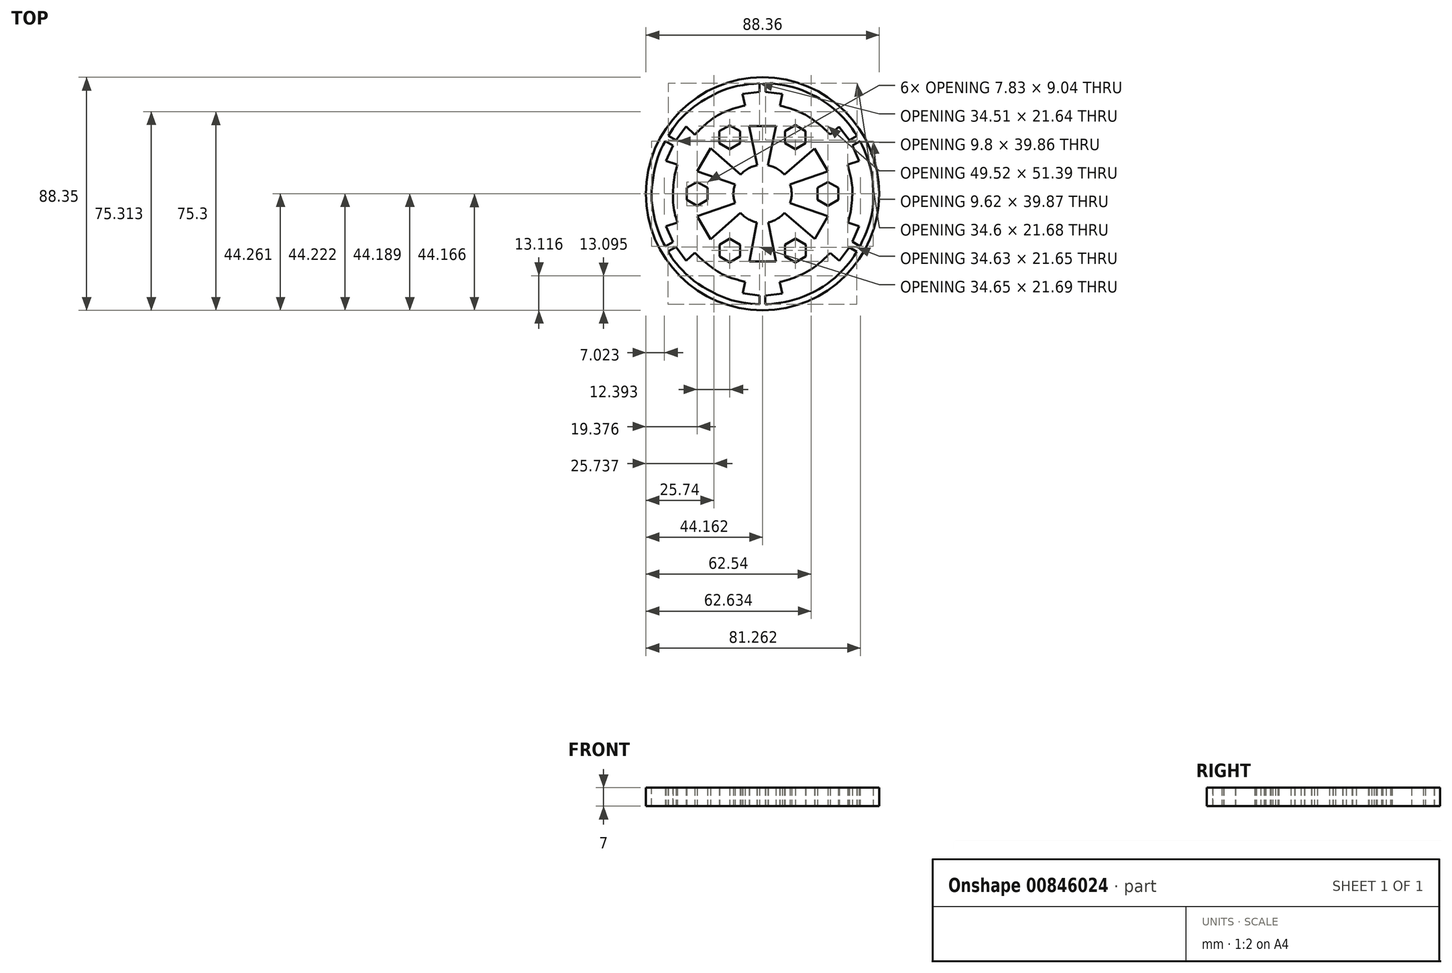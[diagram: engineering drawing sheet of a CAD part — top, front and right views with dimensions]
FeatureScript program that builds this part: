
annotation { "Feature Type Name" : "Feature", "Feature Type Description" : "" }
export const myFeature = defineFeature(function(context is Context, id is Id, definition is map)
    precondition{}
    {
        {
            var Q0;
            Q0=qCreatedBy(makeId("Top.planeOp"),FACE);
            var sketch = newSketch(context, id + "F0", { "sketchPlane" : qUnion([Q0])});
            skLineSegment(sketch, "E0", {"start": v(2.42, -11.3) * mm, "end": v(4.95, -23.85) * mm});
            skLineSegment(sketch, "E1", {"start": v(-2.75, -11.3) * mm, "end": v(-5.12, -23.88) * mm});
            skLineSegment(sketch, "E2", {"start": v(-5.12, -23.88) * mm, "end": v(4.95, -23.85) * mm});
            skLineSegment(sketch, "E3", {"start": v(-10.32, -6.91) * mm, "end": v(-19.92, -15.41) * mm});
            skLineSegment(sketch, "E4", {"start": v(-12.85, -2.44) * mm, "end": v(-24.96, -6.66) * mm});
            skLineSegment(sketch, "E5", {"start": v(-24.96, -6.66) * mm, "end": v(-19.92, -15.41) * mm});
            skLineSegment(sketch, "E6", {"start": v(12.49, -2.45) * mm, "end": v(24.56, -6.66) * mm});
            skLineSegment(sketch, "E7", {"start": v(9.9, -6.97) * mm, "end": v(19.6, -15.3) * mm});
            skLineSegment(sketch, "E8", {"start": v(19.6, -15.3) * mm, "end": v(24.56, -6.66) * mm});
            skLineSegment(sketch, "E9", {"start": v(12.44, 6.2) * mm, "end": v(24.56, 10.39) * mm});
            skLineSegment(sketch, "E10", {"start": v(9.84, 10.64) * mm, "end": v(19.52, 19.04) * mm});
            skLineSegment(sketch, "E11", {"start": v(19.52, 19.04) * mm, "end": v(24.56, 10.39) * mm});
            skLineSegment(sketch, "E12", {"start": v(2.36, 14.93) * mm, "end": v(4.87, 27.52) * mm});
            skLineSegment(sketch, "E13", {"start": v(-2.72, 14.93) * mm, "end": v(-5.3, 27.49) * mm});
            skLineSegment(sketch, "E14", {"start": v(-5.3, 27.49) * mm, "end": v(4.87, 27.52) * mm});
            skLineSegment(sketch, "E15", {"start": v(-10.25, 10.6) * mm, "end": v(-19.89, 19.07) * mm});
            skLineSegment(sketch, "E16", {"start": v(-12.8, 6.18) * mm, "end": v(-24.92, 10.37) * mm});
            skLineSegment(sketch, "E17", {"start": v(-24.92, 10.37) * mm, "end": v(-19.89, 19.07) * mm});
            skLineSegment(sketch, "E18", {"start": v(-1.37, 43.75) * mm, "end": v(-1.37, 40.4) * mm});
            skLineSegment(sketch, "E19", {"start": v(0.97, 43.78) * mm, "end": v(0.97, 40.4) * mm});
            skLineSegment(sketch, "E20", {"start": v(33.82, 20.11) * mm, "end": v(36.73, 21.82) * mm});
            skLineSegment(sketch, "E21", {"start": v(33.82, -16.36) * mm, "end": v(36.72, -18.04) * mm});
            skLineSegment(sketch, "E22", {"start": v(32.7, -18.45) * mm, "end": v(35.5, -20.13) * mm});
            skLineSegment(sketch, "E23", {"start": v(-33, -18.4) * mm, "end": v(-35.94, -20.06) * mm});
            skLineSegment(sketch, "E24", {"start": v(-37.04, -18.08) * mm, "end": v(-34.11, -16.4) * mm});
            skLineSegment(sketch, "E25", {"start": v(-37.05, 21.78) * mm, "end": v(-34.1, 20.13) * mm});
            skLineSegment(sketch, "E26", {"start": v(-35.88, 23.84) * mm, "end": v(-32.98, 22.11) * mm});
            skLineSegment(sketch, "E27", {"start": v(-34.1, 20.13) * mm, "end": v(-36.74, 14.27) * mm});
            skLineSegment(sketch, "E28", {"start": v(-36.74, 14.27) * mm, "end": v(-32.44, 12.84) * mm});
            skLineSegment(sketch, "E29", {"start": v(-32.98, 22.11) * mm, "end": v(-29.18, 27.3) * mm});
            skLineSegment(sketch, "E30", {"start": v(-29.18, 27.3) * mm, "end": v(-25.86, 24.23) * mm});
            skLineSegment(sketch, "E31", {"start": v(-34.11, -16.4) * mm, "end": v(-36.73, -10.52) * mm});
            skLineSegment(sketch, "E32", {"start": v(-36.73, -10.52) * mm, "end": v(-32.44, -9.07) * mm});
            skLineSegment(sketch, "E33", {"start": v(-33, -18.4) * mm, "end": v(-29.14, -23.57) * mm});
            skLineSegment(sketch, "E34", {"start": v(-29.14, -23.57) * mm, "end": v(-25.78, -20.54) * mm});
            skPoint(sketch, "E35.end.orphan", {"position": v(-1.46, -40.1) * mm});
            skPoint(sketch, "E35.start.orphan", {"position": v(-1.46, -36.72) * mm});
            skLineSegment(sketch, "E36", {"start": v(-1.3, -36.72) * mm, "end": v(-1.3, -40.1) * mm});
            skPoint(sketch, "E37.end.orphan", {"position": v(1.01, -40.1) * mm});
            skPoint(sketch, "E37.start.orphan", {"position": v(1.01, -36.72) * mm});
            skLineSegment(sketch, "E38", {"start": v(-1.3, -36.72) * mm, "end": v(-1.46, -36.72) * mm});
            skLineSegment(sketch, "E39", {"start": v(-1.3, -36.72) * mm, "end": v(-7.67, -35.94) * mm});
            skLineSegment(sketch, "E40", {"start": v(-7.67, -35.94) * mm, "end": v(-6.75, -31.52) * mm});
            skLineSegment(sketch, "E41", {"start": v(0.86, -36.72) * mm, "end": v(0.86, -40.1) * mm});
            skLineSegment(sketch, "E42", {"start": v(0.86, -36.72) * mm, "end": v(7.25, -36.02) * mm});
            skLineSegment(sketch, "E43", {"start": v(7.25, -36.02) * mm, "end": v(6.34, -31.59) * mm});
            skLineSegment(sketch, "E44", {"start": v(32.7, -18.45) * mm, "end": v(28.86, -23.6) * mm});
            skLineSegment(sketch, "E45", {"start": v(28.86, -23.6) * mm, "end": v(25.42, -20.65) * mm});
            skLineSegment(sketch, "E46", {"start": v(33.82, -16.36) * mm, "end": v(36.44, -10.53) * mm});
            skLineSegment(sketch, "E47", {"start": v(36.44, -10.53) * mm, "end": v(32.16, -9.1) * mm});
            skLineSegment(sketch, "E48", {"start": v(33.82, 20.11) * mm, "end": v(36.4, 14.22) * mm});
            skLineSegment(sketch, "E49", {"start": v(36.4, 14.22) * mm, "end": v(32.1, 12.82) * mm});
            skLineSegment(sketch, "E50", {"start": v(32.66, 22.1) * mm, "end": v(35.58, 23.8) * mm});
            skLineSegment(sketch, "E51", {"start": v(32.66, 22.1) * mm, "end": v(28.81, 27.25) * mm});
            skLineSegment(sketch, "E52", {"start": v(28.81, 27.25) * mm, "end": v(25.43, 24.28) * mm});
            skLineSegment(sketch, "E53", {"start": v(-1.37, 40.4) * mm, "end": v(-7.76, 39.67) * mm});
            skLineSegment(sketch, "E54", {"start": v(-7.76, 39.67) * mm, "end": v(-6.8, 35.25) * mm});
            skLineSegment(sketch, "E55", {"start": v(0.97, 40.4) * mm, "end": v(7.35, 39.66) * mm});
            skLineSegment(sketch, "E56", {"start": v(7.35, 39.66) * mm, "end": v(6.4, 35.21) * mm});
            skFitSpline(sketch, "E57", {"points": [v(-32.44, -9.07) * mm, v(-33.84, -3.63) * mm, v(-34.08, 1.8) * mm, v(-33.72, 7.26) * mm, v(-32.44, 12.84) * mm], "startDerivative": vector(-6.71, 21.57) * mm, "endDerivative": vector(5.92, 22) * mm});
            skFitSpline(sketch, "E58", {"points": [v(-25.86, 24.23) * mm, v(-21.86, 28.08) * mm, v(-17.87, 31.1) * mm, v(-11.94, 33.88) * mm, v(-6.8, 35.25) * mm], "startDerivative": vector(16.19, 16.08) * mm, "endDerivative": vector(20.55, 4.51) * mm});
            skFitSpline(sketch, "E59", {"points": [v(-25.78, -20.54) * mm, v(-22.24, -23.88) * mm, v(-17.88, -27.2) * mm, v(-13.06, -29.7) * mm, v(-6.75, -31.52) * mm], "startDerivative": vector(14.21, -15.18) * mm, "endDerivative": vector(24.22, -5.87) * mm});
            skFitSpline(sketch, "E60", {"points": [v(6.34, -31.59) * mm, v(10.25, -30.54) * mm, v(15, -28.56) * mm, v(19.43, -26) * mm, v(22.3, -23.6) * mm, v(25.42, -20.65) * mm], "startDerivative": vector(20.1, 4.76) * mm, "endDerivative": vector(16.26, 15.48) * mm});
            skFitSpline(sketch, "E61", {"points": [v(32.16, -9.1) * mm, v(33.4, -3.73) * mm, v(33.82, 1.8) * mm, v(33.82, 4.02) * mm, v(33.31, 7.64) * mm, v(32.1, 12.82) * mm], "startDerivative": vector(6.39, 22.77) * mm, "endDerivative": vector(-6.09, 23.91) * mm});
            skFitSpline(sketch, "E62", {"points": [v(25.43, 24.28) * mm, v(21.95, 27.65) * mm, v(17.67, 30.77) * mm, v(13.95, 32.78) * mm, v(8.52, 34.72) * mm, v(6.4, 35.21) * mm], "startDerivative": vector(-15.56, 16.18) * mm, "endDerivative": vector(-12.9, 2.5) * mm});
            skFitSpline(sketch, "E63", {"points": [v(-35.88, 23.84) * mm, v(-32.44, 28.82) * mm, v(-28.06, 33.25) * mm, v(-23.94, 36.4) * mm, v(-17.87, 39.84) * mm, v(-10.6, 42.49) * mm, v(-1.37, 43.75) * mm], "startDerivative": vector(20.42, 32.39) * mm, "endDerivative": vector(49.13, 4.55) * mm});
            skFitSpline(sketch, "E64", {"points": [v(-37.05, 21.78) * mm, v(-39.75, 16.01) * mm, v(-41.55, 8.23) * mm, v(-42.24, 1.8) * mm, v(-41.64, -4.95) * mm, v(-39.28, -13.47) * mm, v(-37.04, -18.08) * mm], "startDerivative": vector(-18.3, -33.84) * mm, "endDerivative": vector(15.88, -28.7) * mm});
            skFitSpline(sketch, "E65", {"points": [v(-35.94, -20.06) * mm, v(-34.25, -22.77) * mm, v(-31.48, -26.18) * mm, v(-26.4, -30.97) * mm, v(-19.92, -35.06) * mm, v(-13, -38.17) * mm, v(-6.85, -39.55) * mm, v(-1.3, -40.1) * mm], "startDerivative": vector(15, -25.38) * mm, "endDerivative": vector(39.5, -3.13) * mm});
            skPoint(sketch, "E66.1.internal.orphan", {"position": v(2.63, -40.1) * mm});
            skPoint(sketch, "E66.5.internal.orphan", {"position": v(24.36, -32.35) * mm});
            skPoint(sketch, "E66.7.internal.orphan", {"position": v(32.54, -24.74) * mm});
            skFitSpline(sketch, "E67", {"points": [v(0.86, -40.1) * mm, v(2.15, -40.1) * mm, v(5.92, -39.6) * mm, v(9.73, -38.86) * mm, v(14.05, -37.67) * mm, v(19.35, -35.31) * mm, v(23.5, -32.88) * mm, v(27.01, -30.18) * mm, v(30.99, -26.24) * mm, v(33.04, -23.8) * mm, v(35.5, -20.13) * mm], "startDerivative": vector(19.64, -0.97) * mm, "endDerivative": vector(24.32, 37.94) * mm});
            skFitSpline(sketch, "E68", {"points": [v(0.97, 43.78) * mm, v(7.81, 43.04) * mm, v(14.15, 41.33) * mm, v(20.52, 38.42) * mm, v(26.43, 34.35) * mm, v(32, 28.84) * mm, v(35.58, 23.8) * mm], "startDerivative": vector(41.76, -3.24) * mm, "endDerivative": vector(20.77, -31.79) * mm});
            skFitSpline(sketch, "E69", {"points": [v(36.73, 21.82) * mm, v(39.5, 15.56) * mm, v(41.34, 8.48) * mm, v(41.7, 3.2) * mm, v(41.6, -2.96) * mm, v(39.98, -10.44) * mm, v(36.72, -18.04) * mm], "startDerivative": vector(17.68, -36.35) * mm, "endDerivative": vector(-19.56, -41.17) * mm});
            skCircle(sketch, "E70", {"center": v(-0.18, 1.8) * mm, "radius": 44.18 * mm});
            skLineSegment(sketch, "E71", {"start": v(10.23, 5.43) * mm, "end": v(10.17, 5.4) * mm});
            skLineSegment(sketch, "E72", {"start": v(8.08, 9.11) * mm, "end": v(8.03, 9.07) * mm});
            skLineSegment(sketch, "E73", {"start": v(-2.25, 12.63) * mm, "end": v(-2.24, 12.57) * mm});
            skLineSegment(sketch, "E74", {"start": v(1.9, 12.63) * mm, "end": v(1.9, 12.57) * mm});
            skLineSegment(sketch, "E75", {"start": v(-8.5, 9.05) * mm, "end": v(-8.45, 9.01) * mm});
            skLineSegment(sketch, "E76", {"start": v(-10.6, 5.42) * mm, "end": v(-10.54, 5.4) * mm});
            skLineSegment(sketch, "E77", {"start": v(-10.64, -1.67) * mm, "end": v(-10.58, -1.65) * mm});
            skLineSegment(sketch, "E78", {"start": v(-8.56, -5.36) * mm, "end": v(-8.52, -5.32) * mm});
            skLineSegment(sketch, "E79", {"start": v(-2.31, -9.01) * mm, "end": v(-2.3, -8.95) * mm});
            skLineSegment(sketch, "E80", {"start": v(1.96, -9) * mm, "end": v(1.95, -8.95) * mm});
            skLineSegment(sketch, "E81", {"start": v(8.12, -5.44) * mm, "end": v(8.08, -5.4) * mm});
            skLineSegment(sketch, "E82", {"start": v(10.28, -1.68) * mm, "end": v(10.22, -1.66) * mm});
            skCircle(sketch, "E83", {"center": v(-0.18, 1.8) * mm, "radius": 11.03 * mm});
            skLineSegment(sketch, "E84", {"start": v(-10.25, 10.6) * mm, "end": v(-8.5, 9.05) * mm});
            skLineSegment(sketch, "E85", {"start": v(-12.8, 6.18) * mm, "end": v(-10.54, 5.4) * mm});
            skLineSegment(sketch, "E86", {"start": v(-12.85, -2.44) * mm, "end": v(-10.58, -1.65) * mm});
            skLineSegment(sketch, "E87", {"start": v(-10.32, -6.91) * mm, "end": v(-8.52, -5.32) * mm});
            skLineSegment(sketch, "E88", {"start": v(-2.75, -11.3) * mm, "end": v(-2.3, -8.95) * mm});
            skLineSegment(sketch, "E89", {"start": v(2.42, -11.3) * mm, "end": v(1.96, -9) * mm});
            skLineSegment(sketch, "E90", {"start": v(9.9, -6.97) * mm, "end": v(8.12, -5.44) * mm});
            skLineSegment(sketch, "E91", {"start": v(12.49, -2.45) * mm, "end": v(10.28, -1.68) * mm});
            skLineSegment(sketch, "E92", {"start": v(12.44, 6.2) * mm, "end": v(10.23, 5.43) * mm});
            skLineSegment(sketch, "E93", {"start": v(9.84, 10.64) * mm, "end": v(8.08, 9.11) * mm});
            skLineSegment(sketch, "E94", {"start": v(2.36, 14.93) * mm, "end": v(1.9, 12.63) * mm});
            skLineSegment(sketch, "E95", {"start": v(-2.72, 14.93) * mm, "end": v(-2.24, 12.57) * mm});
            skPoint(sketch, "E96.center", {"position": v(0, 0) * mm});
            skLineSegment(sketch, "E97", {"start": v(-19.89, 19.07) * mm, "end": v(-5.3, 27.49) * mm, "construction": true});
            skCircle(sketch, "E98.cCircle", {"center": v(-12.6, 23.28) * mm, "radius": 3.92 * mm, "construction": true});
            skLineSegment(sketch, "E98.0", {"start": v(-8.68, 25.54) * mm, "end": v(-8.68, 21.02) * mm});
            skLineSegment(sketch, "E98.1", {"start": v(-8.68, 21.02) * mm, "end": v(-12.6, 18.76) * mm});
            skLineSegment(sketch, "E98.2", {"start": v(-12.6, 18.76) * mm, "end": v(-16.5, 21.02) * mm});
            skLineSegment(sketch, "E98.3", {"start": v(-16.5, 21.02) * mm, "end": v(-16.5, 25.54) * mm});
            skLineSegment(sketch, "E98.4", {"start": v(-16.5, 25.54) * mm, "end": v(-12.6, 27.8) * mm});
            skLineSegment(sketch, "E98.5", {"start": v(-12.6, 27.8) * mm, "end": v(-8.68, 25.54) * mm});
            skPoint(sketch, "E98.0.midPoint", {"position": v(-8.68, 23.28) * mm});
            skCircle(sketch, "E99.1.0", {"center": v(-24.98, 1.8) * mm, "radius": 3.92 * mm, "construction": true});
            skLineSegment(sketch, "E99.1.1", {"start": v(-24.98, -2.73) * mm, "end": v(-28.9, -0.46) * mm});
            skLineSegment(sketch, "E99.1.2", {"start": v(-28.9, -0.46) * mm, "end": v(-28.9, 4.06) * mm});
            skLineSegment(sketch, "E99.1.3", {"start": v(-28.9, 4.06) * mm, "end": v(-24.98, 6.32) * mm});
            skLineSegment(sketch, "E99.1.4", {"start": v(-24.98, 6.32) * mm, "end": v(-21.07, 4.06) * mm});
            skLineSegment(sketch, "E99.1.5", {"start": v(-21.07, 4.06) * mm, "end": v(-21.07, -0.46) * mm});
            skLineSegment(sketch, "E99.1.6", {"start": v(-21.07, -0.46) * mm, "end": v(-24.98, -2.73) * mm});
            skCircle(sketch, "E99.2.0", {"center": v(-12.57, -19.68) * mm, "radius": 3.92 * mm, "construction": true});
            skLineSegment(sketch, "E99.2.1", {"start": v(-8.66, -21.94) * mm, "end": v(-12.57, -24.2) * mm});
            skLineSegment(sketch, "E99.2.2", {"start": v(-12.57, -24.2) * mm, "end": v(-16.49, -21.94) * mm});
            skLineSegment(sketch, "E99.2.3", {"start": v(-16.49, -21.94) * mm, "end": v(-16.49, -17.42) * mm});
            skLineSegment(sketch, "E99.2.4", {"start": v(-16.49, -17.42) * mm, "end": v(-12.57, -15.16) * mm});
            skLineSegment(sketch, "E99.2.5", {"start": v(-12.57, -15.16) * mm, "end": v(-8.66, -17.42) * mm});
            skLineSegment(sketch, "E99.2.6", {"start": v(-8.66, -17.42) * mm, "end": v(-8.66, -21.94) * mm});
            skCircle(sketch, "E99.3.0", {"center": v(12.23, -19.67) * mm, "radius": 3.92 * mm, "construction": true});
            skLineSegment(sketch, "E99.3.1", {"start": v(16.14, -17.4) * mm, "end": v(16.14, -21.93) * mm});
            skLineSegment(sketch, "E99.3.2", {"start": v(16.14, -21.93) * mm, "end": v(12.23, -24.19) * mm});
            skLineSegment(sketch, "E99.3.3", {"start": v(12.23, -24.19) * mm, "end": v(8.31, -21.93) * mm});
            skLineSegment(sketch, "E99.3.4", {"start": v(8.31, -21.93) * mm, "end": v(8.31, -17.4) * mm});
            skLineSegment(sketch, "E99.3.5", {"start": v(8.31, -17.4) * mm, "end": v(12.23, -15.15) * mm});
            skLineSegment(sketch, "E99.3.6", {"start": v(12.23, -15.15) * mm, "end": v(16.14, -17.4) * mm});
            skCircle(sketch, "E99.4.0", {"center": v(24.62, 1.82) * mm, "radius": 3.92 * mm, "construction": true});
            skLineSegment(sketch, "E99.4.1", {"start": v(24.62, 6.34) * mm, "end": v(28.54, 4.08) * mm});
            skLineSegment(sketch, "E99.4.2", {"start": v(28.54, 4.08) * mm, "end": v(28.54, -0.44) * mm});
            skLineSegment(sketch, "E99.4.3", {"start": v(28.54, -0.44) * mm, "end": v(24.62, -2.7) * mm});
            skLineSegment(sketch, "E99.4.4", {"start": v(24.62, -2.7) * mm, "end": v(20.7, -0.44) * mm});
            skLineSegment(sketch, "E99.4.5", {"start": v(20.7, -0.44) * mm, "end": v(20.7, 4.08) * mm});
            skLineSegment(sketch, "E99.4.6", {"start": v(20.7, 4.08) * mm, "end": v(24.62, 6.34) * mm});
            skCircle(sketch, "E99.5.0", {"center": v(12.21, 23.3) * mm, "radius": 3.92 * mm, "construction": true});
            skLineSegment(sketch, "E99.5.1", {"start": v(8.3, 25.55) * mm, "end": v(12.21, 27.81) * mm});
            skLineSegment(sketch, "E99.5.2", {"start": v(12.21, 27.81) * mm, "end": v(16.13, 25.55) * mm});
            skLineSegment(sketch, "E99.5.3", {"start": v(16.13, 25.55) * mm, "end": v(16.13, 21.03) * mm});
            skLineSegment(sketch, "E99.5.4", {"start": v(16.13, 21.03) * mm, "end": v(12.21, 18.77) * mm});
            skLineSegment(sketch, "E99.5.5", {"start": v(12.21, 18.77) * mm, "end": v(8.3, 21.03) * mm});
            skLineSegment(sketch, "E99.5.6", {"start": v(8.3, 21.03) * mm, "end": v(8.3, 25.55) * mm});
            skSolve(sketch);
        }
        {
            var Q0;
            Q0=makeQuery(id+"F0.imprint","IMPRINT",FACE,{"disambiguationData":[TD([[makeQuery(id+"F0.imprint","IMPRINT",EDGE,{"derivedFrom":sQuery(id+"F0.wireOp",EDGE,"E0")}),1.0]])]});
            extrude(context, id + "F1", {"entities" : qUnion([Q0]), "depth" : 7 * mm, "offsetDistance" : 25 * mm});
        }
    });
